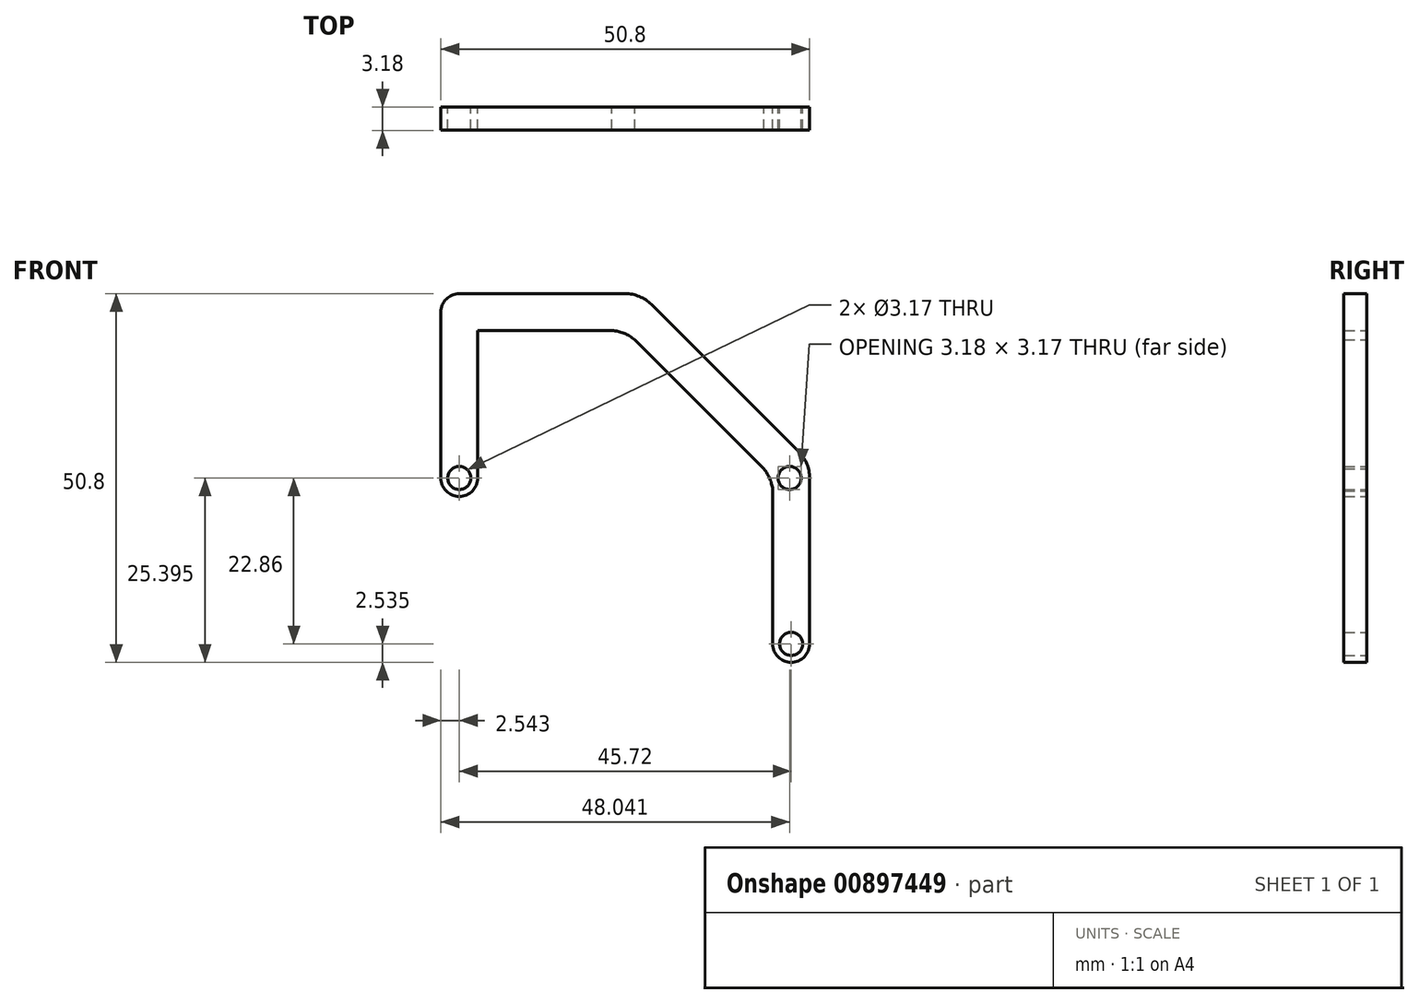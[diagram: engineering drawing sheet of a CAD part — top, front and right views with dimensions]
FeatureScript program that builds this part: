
annotation { "Feature Type Name" : "Feature", "Feature Type Description" : "" }
export const myFeature = defineFeature(function(context is Context, id is Id, definition is map)
    precondition{}
    {
        {
            var Q0;
            Q0=qCreatedBy(makeId("Front.planeOp"),FACE);
            var sketch = newSketch(context, id + "F0", { "sketchPlane" : qUnion([Q0])});
            skLineSegment(sketch, "E0", {"start": v(-37.02, 20.65) * mm, "end": v(-37.02, -4.75) * mm});
            skLineSegment(sketch, "E1", {"start": v(-31.94, 20.65) * mm, "end": v(-31.94, -4.75) * mm});
            skArc(sketch, "E2", {"start": v(-37.02, -4.75) * mm, "mid": v(-34.48, -7.3) * mm, "end": v(-31.94, -4.75) * mm});
            skCircle(sketch, "E3", {"center": v(-34.48, -4.75) * mm, "radius": 1.59 * mm});
            skLineSegment(sketch, "E4", {"start": v(-37.02, 20.65) * mm, "end": v(-31.94, 20.65) * mm});
            skLineSegment(sketch, "E5", {"start": v(-31.94, 20.65) * mm, "end": v(-11.62, 20.65) * mm});
            skLineSegment(sketch, "E6", {"start": v(13.78, -4.75) * mm, "end": v(13.78, -27.61) * mm});
            skLineSegment(sketch, "E7", {"start": v(13.78, -27.61) * mm, "end": v(8.7, -27.61) * mm});
            skLineSegment(sketch, "E8", {"start": v(8.7, -27.61) * mm, "end": v(8.7, -4.75) * mm});
            skLineSegment(sketch, "E9", {"start": v(8.7, -4.75) * mm, "end": v(-11.62, 15.57) * mm});
            skLineSegment(sketch, "E10", {"start": v(-11.62, 15.57) * mm, "end": v(-31.94, 15.57) * mm});
            skLineSegment(sketch, "E11", {"start": v(-8.03, 19.16) * mm, "end": v(12.3, -1.16) * mm});
            skLineSegment(sketch, "E12", {"start": v(-11.62, 20.65) * mm, "end": v(-11.62, 15.57) * mm});
            skLineSegment(sketch, "E13", {"start": v(-8.03, 19.16) * mm, "end": v(-11.62, 15.57) * mm});
            skLineSegment(sketch, "E14", {"start": v(8.7, -4.75) * mm, "end": v(12.3, -1.16) * mm});
            skLineSegment(sketch, "E15", {"start": v(8.7, -4.75) * mm, "end": v(13.78, -4.75) * mm});
            skArc(sketch, "E16", {"start": v(-8.03, 19.16) * mm, "mid": v(-9.67, 20.26) * mm, "end": v(-11.62, 20.65) * mm});
            skArc(sketch, "E17", {"start": v(13.78, -4.75) * mm, "mid": v(13.4, -2.81) * mm, "end": v(12.3, -1.16) * mm});
            skArc(sketch, "E18", {"start": v(8.7, -27.61) * mm, "mid": v(11.24, -30.15) * mm, "end": v(13.78, -27.61) * mm});
            skLineSegment(sketch, "E19.bottom", {"start": v(8.7, -27.61) * mm, "end": v(13.78, -27.61) * mm});
            skLineSegment(sketch, "E19.top", {"start": v(8.7, -30.15) * mm, "end": v(13.78, -30.15) * mm});
            skLineSegment(sketch, "E19.left", {"start": v(8.7, -27.61) * mm, "end": v(8.7, -30.15) * mm});
            skLineSegment(sketch, "E19.right", {"start": v(13.78, -27.61) * mm, "end": v(13.78, -30.15) * mm});
            skLineSegment(sketch, "E20", {"start": v(8.7, -4.75) * mm, "end": v(13.4, -2.81) * mm, "construction": true});
            skCircle(sketch, "E21", {"center": v(11.24, -27.61) * mm, "radius": 1.59 * mm});
            skLineSegment(sketch, "E22", {"start": v(-9.67, 20.26) * mm, "end": v(-11.62, 15.57) * mm, "construction": true});
            skArc(sketch, "E23", {"start": v(-10.32, 14.27) * mm, "mid": v(-11.77, 15.19) * mm, "end": v(-13.45, 15.57) * mm});
            skLineSegment(sketch, "E24", {"start": v(-11.77, 15.19) * mm, "end": v(-11.62, 15.57) * mm, "construction": true});
            skArc(sketch, "E25", {"start": v(8.7, -6.51) * mm, "mid": v(8.33, -4.91) * mm, "end": v(7.46, -3.51) * mm});
            skLineSegment(sketch, "E26", {"start": v(8.33, -4.91) * mm, "end": v(8.7, -4.75) * mm, "construction": true});
            skLineSegment(sketch, "E27", {"start": v(-26.86, 15.57) * mm, "end": v(-26.86, 20.65) * mm, "construction": true});
            skPoint(sketch, "E28", {"position": v(-34.48, 20.65) * mm});
            skPoint(sketch, "E29", {"position": v(-37.02, 18.1) * mm});
            skArc(sketch, "E30", {"start": v(-34.48, 20.65) * mm, "mid": v(-36.27, 19.9) * mm, "end": v(-37.02, 18.1) * mm});
            skLineSegment(sketch, "E31", {"start": v(-37.02, 20.65) * mm, "end": v(-31.94, 15.57) * mm, "construction": true});
            skLineSegment(sketch, "E32", {"start": v(-31.94, 15.57) * mm, "end": v(-28.35, 11.97) * mm, "construction": true});
            skPoint(sketch, "E33", {"position": v(-29.4, 15.57) * mm});
            skPoint(sketch, "E34", {"position": v(-31.94, 13.03) * mm});
            skArc(sketch, "E35", {"start": v(-29.4, 15.57) * mm, "mid": v(-31.2, 14.82) * mm, "end": v(-31.94, 13.03) * mm});
            skLineSegment(sketch, "E36", {"start": v(-37.02, -4.75) * mm, "end": v(-31.94, -4.75) * mm, "construction": true});
            skPoint(sketch, "E37", {"position": v(8.26, -4.75) * mm});
            skPoint(sketch, "E38", {"position": v(13.78, -4.75) * mm});
            skLineSegment(sketch, "E39", {"start": v(8.26, -4.75) * mm, "end": v(13.78, -4.75) * mm, "construction": true});
            skCircle(sketch, "E40", {"center": v(11.02, -4.75) * mm, "radius": 1.59 * mm});
            skSolve(sketch);
        }
        {
            var Q0;
            {var subQ0=sQuery(id+"F0.wireOp",EDGE,"aPGU2UQI-rGk2-vtnC-eSC2-bPblPhgpPRlq");Q0=makeQuery(id+"F0.imprint","IMPRINT",FACE,{"disambiguationData":[TD([[makeQuery(id+"F0.imprint","IMPRINT",EDGE,{"derivedFrom":subQ0}),-1.0]])]});}
            var Q1;
            {var subQ3=sQuery(id+"F0.wireOp",EDGE,"E25");Q1=makeQuery(id+"F0.imprint","IMPRINT",FACE,{"disambiguationData":[TD([[makeQuery(id+"F0.imprint","IMPRINT",EDGE,{"derivedFrom":subQ3}),-1.0]])]});}
            var Q2;
            {var subQ3=sQuery(id+"F0.wireOp",EDGE,"E23");Q2=makeQuery(id+"F0.imprint","IMPRINT",FACE,{"disambiguationData":[TD([[makeQuery(id+"F0.imprint","IMPRINT",EDGE,{"derivedFrom":subQ3}),-1.0]])]});}
            var Q3;
            Q3=makeQuery(id+"F0.imprint","IMPRINT",FACE,{"disambiguationData":[TD([[makeQuery(id+"F0.imprint","IMPRINT",EDGE,{"derivedFrom":sQuery(id+"F0.wireOp",EDGE,"E12")}),1.0]])]});
            var Q4;
            {var subQ4=sQuery(id+"F0.wireOp",EDGE,"E17");Q4=makeQuery(id+"F0.imprint","IMPRINT",FACE,{"disambiguationData":[TD([[makeQuery(id+"F0.imprint","IMPRINT",EDGE,{"derivedFrom":subQ4}),1.0]])]});}
            var Q5;
            {var subQ4=sQuery(id+"F0.wireOp",EDGE,"E2");Q5=makeQuery(id+"F0.imprint","IMPRINT",FACE,{"disambiguationData":[TD([[makeQuery(id+"F0.imprint","IMPRINT",EDGE,{"derivedFrom":subQ4}),1.0]])]});}
            var Q6;
            {var subQ4=sQuery(id+"F0.wireOp",EDGE,"E5");Q6=makeQuery(id+"F0.imprint","IMPRINT",FACE,{"disambiguationData":[TD([[makeQuery(id+"F0.imprint","IMPRINT",EDGE,{"derivedFrom":subQ4}),-1.0]])]});}
            var Q7;
            {var subQ1=sQuery(id+"F0.wireOp",EDGE,"E7");var subQ4=sQuery(id+"F0.wireOp",EDGE,"E21");var subQ6=makeQuery(id+"F0.imprint","INTERSECT",VERTEX,{"disambiguationData":[OD(0.0)],"derivedFrom":[subQ1,subQ4]});Q7=makeQuery(id+"F0.imprint","IMPRINT",FACE,{"disambiguationData":[TD([[makeQuery(id+"F0.imprint","IMPRINT",EDGE,{"disambiguationData":[TD([[subQ6,1.0]])],"derivedFrom":subQ4}),-1.0]])]});}
            var Q8;
            {var subQ7=sQuery(id+"F0.wireOp",EDGE,"E6");Q8=makeQuery(id+"F0.imprint","IMPRINT",FACE,{"disambiguationData":[TD([[makeQuery(id+"F0.imprint","IMPRINT",EDGE,{"derivedFrom":subQ7}),-1.0]])]});}
            var Q9;
            {var subQ4=sQuery(id+"F0.wireOp",EDGE,"E11");Q9=makeQuery(id+"F0.imprint","IMPRINT",FACE,{"disambiguationData":[TD([[makeQuery(id+"F0.imprint","IMPRINT",EDGE,{"derivedFrom":subQ4}),-1.0]])]});}
            var Q10;
            {var subQ1=sQuery(id+"F0.wireOp",EDGE,"E14");var subQ3=sQuery(id+"F0.wireOp",EDGE,"i9RWTD9w-XTGB-5wVy-bsk0-Z6kVNGMFFUp4");var subQ4=makeQuery(id+"F0.imprint","INTERSECT",VERTEX,{"disambiguationData":[OD(0.0)],"derivedFrom":[subQ1,subQ3]});Q10=makeQuery(id+"F0.imprint","IMPRINT",FACE,{"disambiguationData":[TD([[makeQuery(id+"F0.imprint","IMPRINT",EDGE,{"disambiguationData":[TD([[subQ4,-1.0]])],"derivedFrom":subQ3}),-1.0]])]});}
            extrude(context, id + "F1", {"entities" : qUnion([Q0, Q1, Q2, Q3, Q4, Q5, Q6, Q7, Q8, Q9, Q10]), "depth" : 3.17 * mm, "offsetDistance" : 25.4 * mm});
        }
    });
